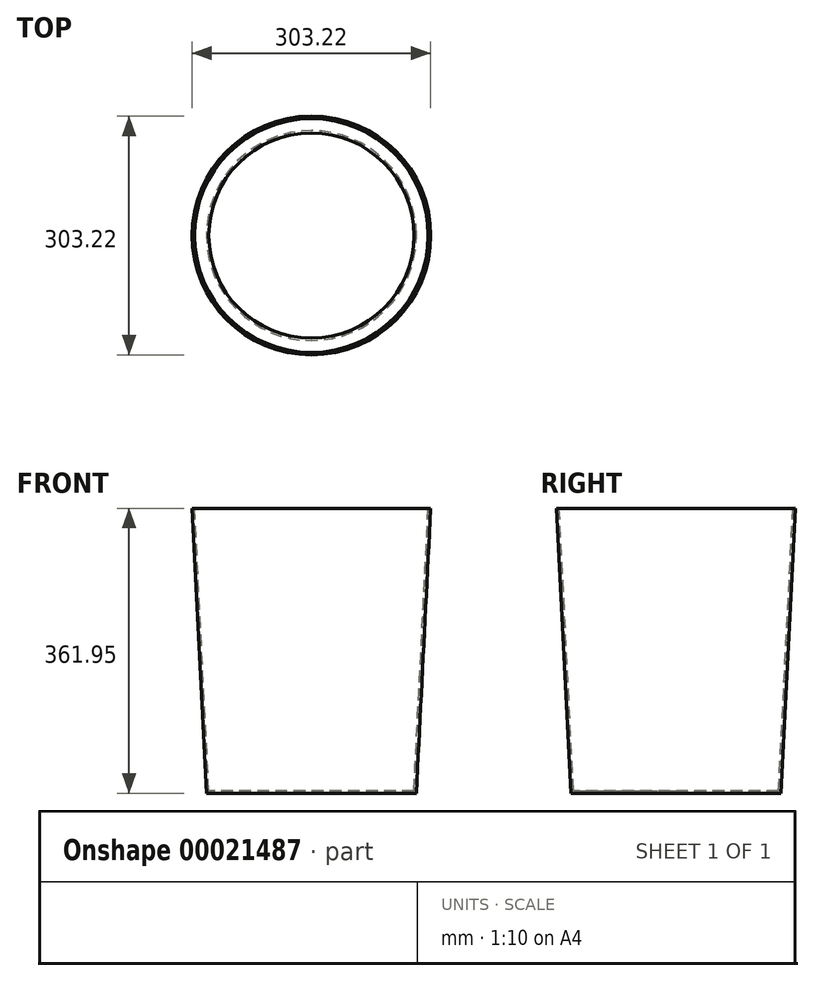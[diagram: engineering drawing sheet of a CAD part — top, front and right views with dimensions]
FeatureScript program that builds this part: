
annotation { "Feature Type Name" : "Feature", "Feature Type Description" : "" }
export const myFeature = defineFeature(function(context is Context, id is Id, definition is map)
    precondition{}
    {
        {
            var Q0;
            Q0=qCreatedBy(makeId("Front.planeOp"),FACE);
            var sketch = newSketch(context, id + "F0", { "sketchPlane" : qUnion([Q0])});
            skLineSegment(sketch, "E0", {"start": v(0, 0) * mm, "end": v(133.35, 0) * mm});
            skLineSegment(sketch, "E1", {"start": v(133.35, 0) * mm, "end": v(151.6, 361.95) * mm});
            skLineSegment(sketch, "E2", {"start": v(151.6, 361.95) * mm, "end": v(0, 361.95) * mm});
            skLineSegment(sketch, "E3", {"start": v(0, 361.95) * mm, "end": v(0, 0) * mm});
            skLineSegment(sketch, "E4", {"start": v(0, 0) * mm, "end": v(0, -74.22) * mm, "construction": true});
            skSolve(sketch);
        }
        {
            var Q0;
            Q0=qSketchRegion(id+"F0",true);
            var Q1;
            Q1=sQuery(id+"F0.wireOp",EDGE,"E4");
            revolve(context, id + "F1", {"entities" : qUnion([Q0]), "axis" : qUnion([Q1]), "revolveType" : RevolveType.FULL});
        }
        {
            var Q0;
            Q0=makeQuery(id+"F1.opRevolve","SWEPT_FACE",FACE,{"disambiguationData":[OSD([sQuery(id+"F0.wireOp",EDGE,"E2")])]});
            shell(context, id + "F2", {"entities" : qUnion([Q0]), "thickness" : 3.17 * mm});
        }
    });
